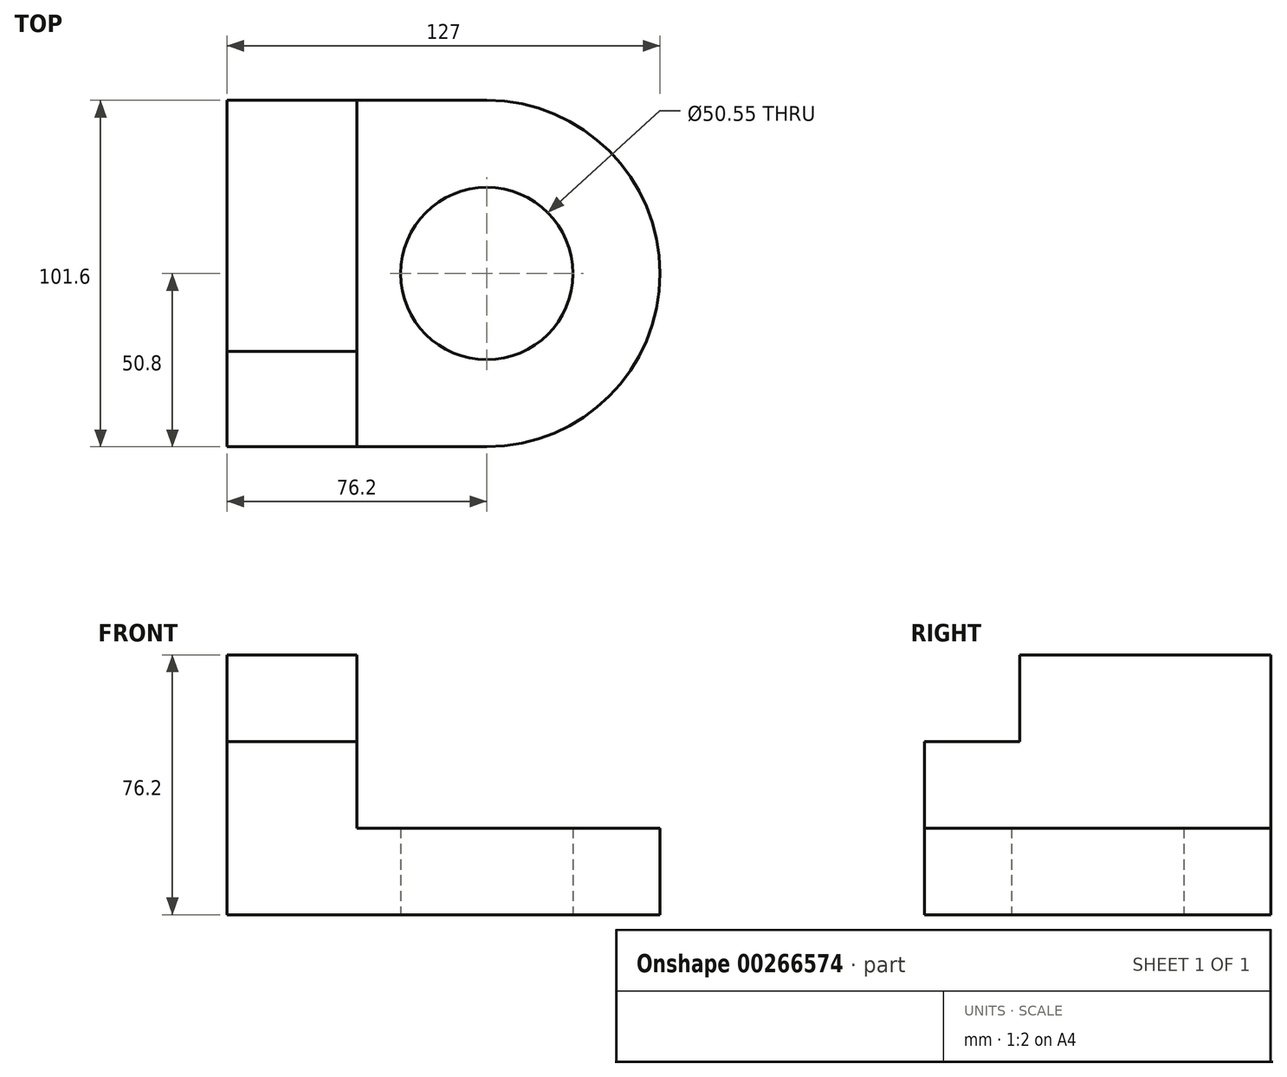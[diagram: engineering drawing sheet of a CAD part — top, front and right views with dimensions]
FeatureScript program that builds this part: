
annotation { "Feature Type Name" : "Feature", "Feature Type Description" : "" }
export const myFeature = defineFeature(function(context is Context, id is Id, definition is map)
    precondition{}
    {
        {
            var Q0;
            Q0=qCreatedBy(makeId("Top.planeOp"),FACE);
            var sketch = newSketch(context, id + "F0", { "sketchPlane" : qUnion([Q0])});
            skLineSegment(sketch, "E0.bottom", {"start": v(-76.2, 50.8) * mm, "end": v(0, 50.8) * mm});
            skLineSegment(sketch, "E0.top", {"start": v(-76.2, -50.8) * mm, "end": v(0, -50.8) * mm});
            skLineSegment(sketch, "E0.left", {"start": v(-76.2, 50.8) * mm, "end": v(-76.2, -50.8) * mm});
            skLineSegment(sketch, "E0.right", {"start": v(0, 50.8) * mm, "end": v(0, -50.8) * mm});
            skSolve(sketch);
        }
        {
            var Q0;
            Q0=qCreatedBy(makeId("Top.planeOp"),FACE);
            var sketch = newSketch(context, id + "F1", { "sketchPlane" : qUnion([Q0])});
            skCircle(sketch, "E1", {"center": v(0, 0) * mm, "radius": 50.8 * mm});
            skSolve(sketch);
        }
        {
            var Q0;
            Q0=makeQuery(id+"F0.imprint","IMPRINT",FACE,{"disambiguationData":[TD([[makeQuery(id+"F0.imprint","IMPRINT",EDGE,{"derivedFrom":sQuery(id+"F0.wireOp",EDGE,"E0.bottom")}),-1.0]])]});
            extrude(context, id + "F2", {"entities" : qUnion([Q0]), "depth" : 25.4 * mm});
        }
        {
            var Q0;
            Q0=makeQuery(id+"F1.imprint","IMPRINT",FACE,{"disambiguationData":[TD([[makeQuery(id+"F1.imprint","IMPRINT",EDGE,{"derivedFrom":sQuery(id+"F1.wireOp",EDGE,"E1")}),1.0]])]});
            extrude(context, id + "F3", {"entities" : qUnion([Q0]), "operationType" : NewBodyOperationType.ADD, "depth" : 25.4 * mm});
        }
        {
            var Q0;
            Q0=qCreatedBy(makeId("Top.planeOp"),FACE);
            var sketch = newSketch(context, id + "F4", { "sketchPlane" : qUnion([Q0])});
            skCircle(sketch, "E2", {"center": v(0, 0) * mm, "radius": 25.28 * mm});
            skSolve(sketch);
        }
        {
            var Q0;
            Q0 = qSketchRegion(id + "F4", true);
            extrude(context, id + "F5", {"entities" : qUnion([Q0]), "operationType" : NewBodyOperationType.REMOVE, "endBound" : BoundingType.THROUGH_ALL, "depth" : 25.4 * mm});
        }
        {
            var Q0;
            Q0=qCreatedBy(makeId("Top.planeOp"),FACE);
            var sketch = newSketch(context, id + "F6", { "sketchPlane" : qUnion([Q0])});
            skLineSegment(sketch, "E3.bottom", {"start": v(-76.2, 50.8) * mm, "end": v(-38.1, 50.8) * mm});
            skLineSegment(sketch, "E3.top", {"start": v(-76.2, -50.8) * mm, "end": v(-38.1, -50.8) * mm});
            skLineSegment(sketch, "E3.left", {"start": v(-76.2, 50.8) * mm, "end": v(-76.2, -50.8) * mm});
            skLineSegment(sketch, "E3.right", {"start": v(-38.1, 50.8) * mm, "end": v(-38.1, -50.8) * mm});
            skSolve(sketch);
        }
        {
            var Q0;
            Q0 = qSketchRegion(id + "F6", true);
            extrude(context, id + "F7", {"entities" : qUnion([Q0]), "operationType" : NewBodyOperationType.ADD, "depth" : 50.8 * mm});
        }
        {
            var Q0;
            Q0=qCreatedBy(makeId("Top.planeOp"),FACE);
            var sketch = newSketch(context, id + "F8", { "sketchPlane" : qUnion([Q0])});
            skLineSegment(sketch, "E4.bottom", {"start": v(-76.2, 50.8) * mm, "end": v(-38.1, 50.8) * mm});
            skLineSegment(sketch, "E4.top", {"start": v(-76.2, -22.83) * mm, "end": v(-38.1, -22.83) * mm});
            skLineSegment(sketch, "E4.left", {"start": v(-76.2, 50.8) * mm, "end": v(-76.2, -22.83) * mm});
            skLineSegment(sketch, "E4.right", {"start": v(-38.1, 50.8) * mm, "end": v(-38.1, -22.83) * mm});
            skSolve(sketch);
        }
        {
            var Q0;
            Q0 = qSketchRegion(id + "F8", true);
            extrude(context, id + "F9", {"entities" : qUnion([Q0]), "operationType" : NewBodyOperationType.ADD, "depth" : 76.2 * mm});
        }
    });
